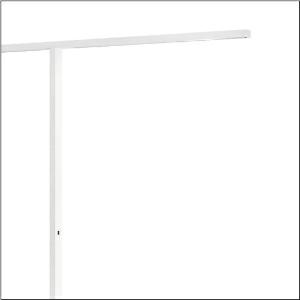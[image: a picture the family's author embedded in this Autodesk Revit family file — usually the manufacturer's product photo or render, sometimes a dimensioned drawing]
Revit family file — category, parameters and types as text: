
# Revit family: silica_r__11_floor_duo_5mx51bs8wzk00006xx_4f95
name_source: partatom
category: Lighting Fixtures
units: mm (PartAtom-declared; Revit-internal decimal feet)

## family parameters
Cut with Voids When Loaded = No
Host = Face
Light Source = No
Part Type = Normal
Room Calculation Point = No
Round Connector Dimension = Use Diameter
Shared = No

## types (1)
- --- (1 x LED, 3970 lm / 8500 lm, 24.1 W / 53.2 W, 4000K)
    Apparent Load = 155 VA
    CIE Flux Codes = 82 97 100 100 100 / - - - 0 100
    Color Rendering = 80
    Color Temperature = 4000K
    Default Elevation = 1800 mm
    Description = Silica® 11 Floor duo, floorstanding luminaire, of PMMA, primary optical cover: cover panel, of PMMA, light emission: indirect/direct distribution, primary light characteristic: symmetric, installation type: not mounted, LED, rated luminous flux: 24.930lm, luminous efficacy: 161lm/W, light colour: 840, colour temperature: 4000K, daylight-dependent control, mains connection: 230V, AC, 50Hz, connection cable pre-assembled, cable length: 3m, rated input power: 155W, luminaire head, rectangular, rounded, of aluminium, coated, traffic white (RAL 9016), supporting column, angular, of aluminium, coated, traffic white (RAL 9016), baseplate, of steel, coated, traffic white (RAL 9016), length: 2.598mm, width: 65mm, protection rating (complete): IP20, insulation class (complete): insulation class I (protective earthing), certification: CE, permissible operating ambient temperature: 0..+35°C, standard: EN 50419, packaging unit: 1 piece
    Height = 40 mm  [stored 0.131234 ft]
    Lamp = 1 x LED
    Lamp Light Flux = 3970 lm / 8500 lm
    Lamp Power = 24.1 W / 53.2 W
    Lamp count = 1
    Length = 2598 mm
    Luminous efficacy = 161 lm/W
    Manufacturer = Siteco
    ModVariant = No
    Model = 5MX51BS8WZK00006XX
    Mounting Place = Floor
    Mounting Type = Freestanding
    Number of Poles = 1
    OnlyDefault = Yes
    Power Factor = 1
    Product Name = Silica® 11 Floor duo
    Product group = floorstanding luminaire
    ProductGroupID = 1301
    Protection Class = Protection class I
    Protection Degree = IP 20
    RLX_Detail_Level = 1
    RLX_Emergency_Light_Flux = 0 lm
    RLX_Emergency_Type = 0
    RLX_Emergency_Type_DB = No
    RlxData = <blob elided: 19149 chars, md5=b55a1d8e>
    Socket = socket
    Standby Power = 0 W
    System Light Flux = 24940 lm
    System Power = 155 W
    Type Comments = factory setting: direct and indirect light
    Type Image = l_1004652.jpg
    URL = http://relux.com
    VarID = @adj_156025
    Voltage = 0 V
    Weight = 0.00 kg
    Width = 65 mm

note: [stored X ft] marks values corroborated as IEEE doubles in the binary element streams (Revit-internal decimal feet)

## geometry (parser evidence)
native form markers: Blend x4, Sweep x19
no freeform markers — native parametric forms only
